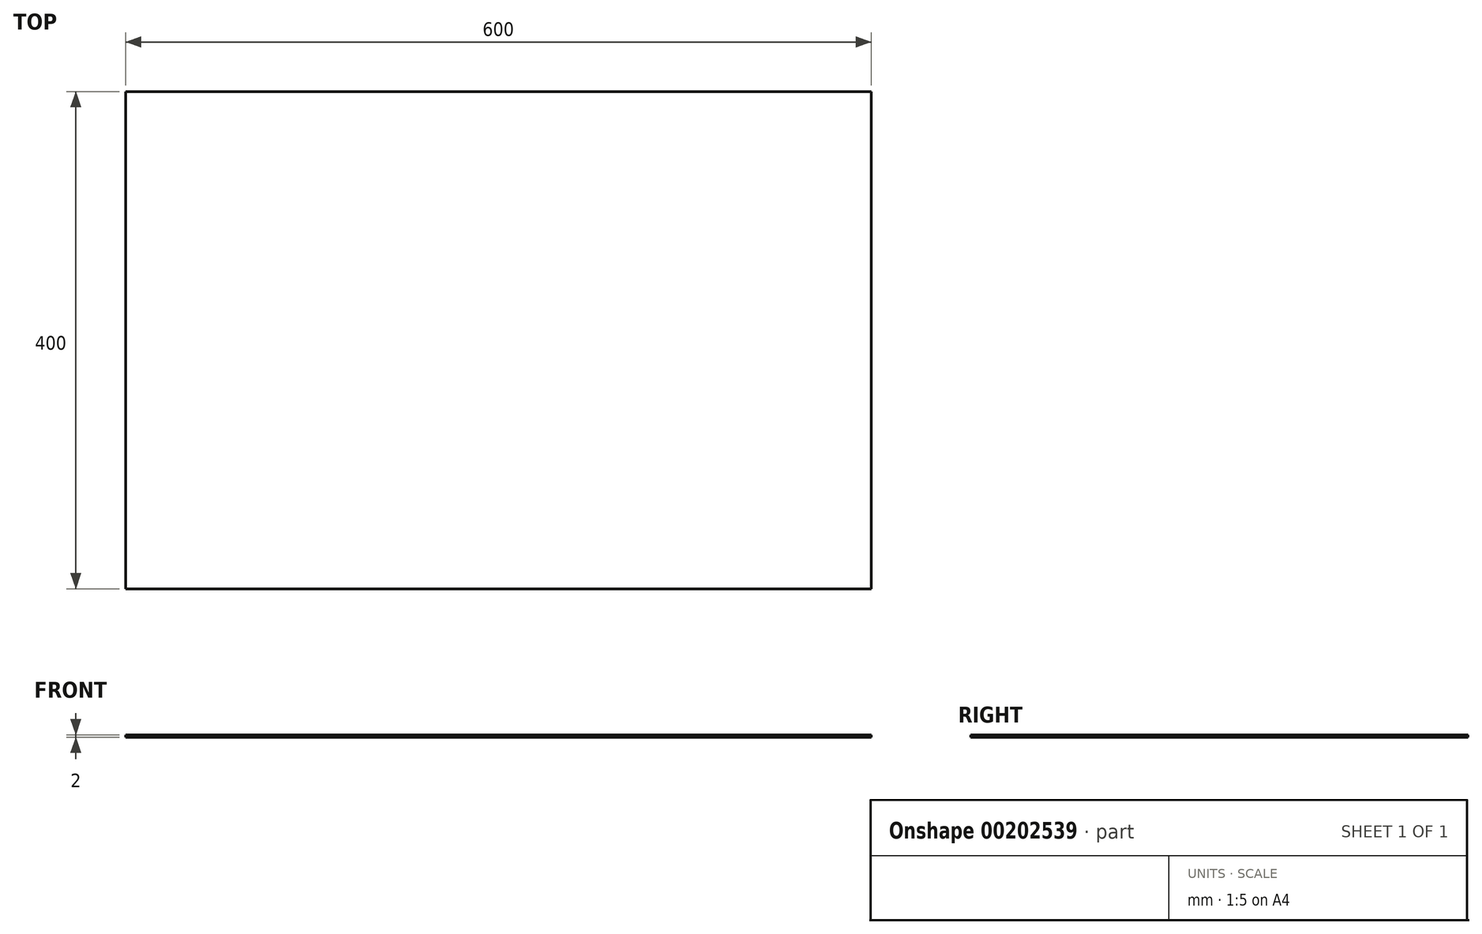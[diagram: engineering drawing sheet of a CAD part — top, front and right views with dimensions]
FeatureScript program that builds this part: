
annotation { "Feature Type Name" : "Feature", "Feature Type Description" : "" }
export const myFeature = defineFeature(function(context is Context, id is Id, definition is map)
    precondition{}
    {
        {
            var Q0;
            Q0=qCreatedBy(makeId("Top.planeOp"),FACE);
            var sketch = newSketch(context, id + "F0", { "sketchPlane" : qUnion([Q0])});
            skLineSegment(sketch, "E0.bottom", {"start": v(-276.3, -87.4) * mm, "end": v(323.7, -87.4) * mm});
            skLineSegment(sketch, "E0.top", {"start": v(-276.3, 312.6) * mm, "end": v(323.7, 312.6) * mm});
            skLineSegment(sketch, "E0.left", {"start": v(-276.3, -87.4) * mm, "end": v(-276.3, 312.6) * mm});
            skLineSegment(sketch, "E0.right", {"start": v(323.7, -87.4) * mm, "end": v(323.7, 312.6) * mm});
            skSolve(sketch);
        }
        {
            var Q0;
            Q0=makeQuery(id+"F0.imprint","IMPRINT",FACE,{"disambiguationData":[TD([[makeQuery(id+"F0.imprint","IMPRINT",EDGE,{"derivedFrom":sQuery(id+"F0.wireOp",EDGE,"E0.bottom")}),1.0]])]});
            extrude(context, id + "F1", {"entities" : qUnion([Q0]), "depth" : 2 * mm});
        }
    });
